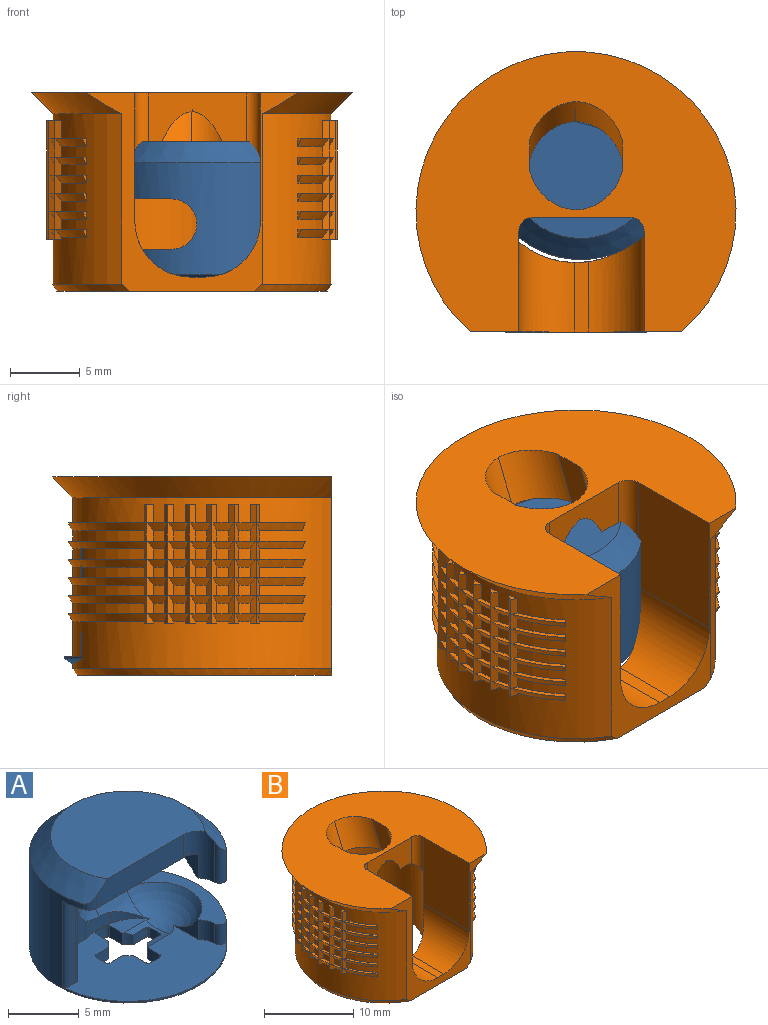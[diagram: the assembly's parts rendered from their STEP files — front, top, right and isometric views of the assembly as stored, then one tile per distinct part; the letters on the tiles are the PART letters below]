
ASSEMBLY  parts=2 mates=1
PART A: 62 faces, bbox 14.4x14.4x10.8 mm
  f0: cone r=6.37mm half-angle=55deg, axis (0,0,1), area 59.3mm2, adj f4,f50
  f1: sphere r=3.61mm, area 17.9mm2, adj f3,f6,f8,f10,f19,f29,f32
  f2: cone r=6.22mm half-angle=45deg, axis (0,0,-1), area 57.3mm2, adj f4,f36,f49,f51,f52,f53,f56
  f3: cone r=3.61mm half-angle=0deg, axis (-1,0,0), area 2.6mm2, adj f1,f8,f39,f40,f41,f42,f43,f44
  f4: cylinder r=6.98mm len=13.95mm, axis (0,0,1), area 160.7mm2, adj f0,f2,f8,f11,f18,f32,f36,f51
  f5: cylinder r=6.91mm len=2.63mm, axis (0,0,-1), area 4.8mm2, adj f7,f11,f12,f59,f60
  f6: cylinder r=3.65mm len=0.52mm, axis (0,0,-1), area 0mm2, adj f1,f8,f10
  f7: cylinder r=3.65mm len=3.82mm, axis (0,0,-1), area 4.6mm2, adj f5,f9,f11,f58,f60
  f8: plane 12.24x9.74mm, normal (0,0,1), area 68.7mm2, adj f1,f3,f4,f6,f10,f12,f13,f14
  f9: plane 2.51x2.4mm, normal (-1,-0.02,0), area 2.7mm2, adj f7,f11,f53,f57,f58
  f10: plane 1.99x1.7mm, normal (-1,-0.02,0), area 1.6mm2, adj f1,f6,f8,f32,f34
  f11: plane 10.92x5.9mm, normal (0,0,-1), area 50.1mm2, adj f4,f5,f7,f9,f12,f13,f14,f15
  f12: plane 7.4x2.64mm, normal (0,-1,0), area 17.4mm2, adj f5,f8,f11,f13,f20,f59
  f13: cylinder r=1mm len=7.4mm, axis (0,0,-1), area 9mm2, adj f8,f11,f12,f14
  f14: cylinder r=5.6mm len=7.4mm, axis (0,0,-1), area 14.7mm2, adj f8,f11,f13,f15
  f15: plane 7.4x0.4mm, normal (1,0,0), area 3mm2, adj f8,f11,f14,f16
  f16: cylinder r=0.3mm len=7.4mm, axis (0,0,-1), area 3.5mm2, adj f8,f11,f15,f17
  f17: plane 7.4x0.76mm, normal (0,-1,0), area 5.6mm2, adj f8,f11,f16,f18
  f18: cylinder r=0.3mm len=7.4mm, axis (0,0,-1), area 3.4mm2, adj f4,f8,f11,f17
  f19: cylinder r=3.65mm len=2.35mm, axis (0,0,-1), area 1.4mm2, adj f1,f8,f20,f29
  f20: cylinder r=6.91mm len=2.63mm, axis (0,0,-1), area 3.2mm2, adj f8,f12,f19,f29,f59
  f21: cylinder r=2.75mm len=1.08mm, axis (0,0,1), area 1.1mm2, adj f8,f22,f37,f50
  f22: cylinder r=0.2mm len=1mm, axis (0,0,1), area 0.3mm2, adj f8,f21,f23,f50
  f23: plane 1.29x1mm, normal (1,0,0), area 1.3mm2, adj f8,f22,f24,f50
  f24: cylinder r=1.4mm len=1mm, axis (0,0,1), area 0.7mm2, adj f8,f23,f25,f50
  f25: plane 1.29x1mm, normal (0,-1,0), area 1.3mm2, adj f8,f24,f26,f50
  f26: cylinder r=0.2mm len=1mm, axis (0,0,1), area 0.3mm2, adj f8,f25,f27,f50
  f27: cylinder r=2.75mm len=1.08mm, axis (0,0,1), area 1.1mm2, adj f8,f26,f28,f50
  f28: cylinder r=0.2mm len=1mm, axis (0,0,1), area 0.3mm2, adj f8,f27,f30,f50
  f29: cone r=3.61mm half-angle=0deg, axis (-1,0,0), area 3.9mm2, adj f1,f19,f20,f32,f59,f61
  f30: plane 1.29x1mm, normal (0,1,0), area 1.3mm2, adj f8,f28,f31,f50
  f31: cylinder r=1.4mm len=1mm, axis (0,0,1), area 0.7mm2, adj f8,f30,f33,f50
  f32: plane 11.71x6.98mm, normal (0,0,1), area 27.4mm2, adj f1,f4,f10,f29,f34,f54,f55,f61
  f33: plane 1.29x1mm, normal (1,0,0), area 1.3mm2, adj f8,f31,f35,f50
  f34: cylinder r=1.5mm len=1.7mm, axis (0,0,-1), area 2mm2, adj f8,f10,f32,f55
  f35: cylinder r=0.2mm len=1mm, axis (0,0,1), area 0.3mm2, adj f8,f33,f48,f50
  f36: cylinder r=0.8mm len=1.01mm, axis (0,0,-1), area 0.8mm2, adj f2,f4,f11,f49
  f37: cylinder r=0.2mm len=1mm, axis (0,0,1), area 0.3mm2, adj f8,f21,f38,f50
  f38: plane 1.29x1mm, normal (-1,0,0), area 1.3mm2, adj f8,f37,f39,f50
  f39: cylinder r=1.4mm len=1mm, axis (0,0,1), area 0.7mm2, adj f3,f8,f38,f40,f50
  f40: plane 1.29x0.86mm, normal (0,-1,0), area 1.1mm2, adj f3,f39,f41,f50
  f41: cylinder r=0.2mm len=0.86mm, axis (0,0,1), area 0.2mm2, adj f3,f40,f42,f50
  f42: cylinder r=2.75mm len=1.08mm, axis (0,0,1), area 0.9mm2, adj f3,f41,f43,f50
  f43: cylinder r=0.2mm len=0.86mm, axis (0,0,1), area 0.2mm2, adj f3,f42,f44,f50
  f44: plane 1.29x0.86mm, normal (0,1,0), area 1.1mm2, adj f3,f43,f45,f50
  f45: cylinder r=1.4mm len=1mm, axis (0,0,1), area 0.7mm2, adj f3,f8,f44,f46,f50
  f46: plane 1.29x1mm, normal (-1,0,0), area 1.3mm2, adj f8,f45,f47,f50
  f47: cylinder r=0.2mm len=1mm, axis (0,0,1), area 0.3mm2, adj f8,f46,f48,f50
  f48: cylinder r=2.75mm len=1.08mm, axis (0,0,1), area 1.1mm2, adj f8,f35,f47,f50
  f49: plane 8.79x2mm, normal (0,-1,0), area 17mm2, adj f2,f11,f36,f53,f56
  f50: plane 11.52x11.52mm, normal (0,0,-1), area 90.4mm2, adj f0,f21,f22,f23,f24,f25,f26,f27
  f51: cylinder r=0.5mm len=3.47mm, axis (0,0,-1), area 3.7mm2, adj f2,f4,f52,f57
  f52: plane 3.49x0.03mm, normal (-1,0,0), area 0.1mm2, adj f2,f51,f53,f57
  f53: cylinder r=1.5mm len=4.1mm, axis (0,0,-1), area 7mm2, adj f2,f9,f11,f49,f52,f56,f57
  f54: cylinder r=0.5mm len=1.7mm, axis (0,0,-1), area 2.1mm2, adj f4,f8,f32,f55
  f55: plane 1.7x0.03mm, normal (-1,0,0), area 0.1mm2, adj f8,f32,f34,f54
  f56: plane 10.95x8.96mm, normal (0,0,1), area 75.9mm2, adj f2,f49,f53
  f57: plane 11.71x6.98mm, normal (0,0,-1), area 28.8mm2, adj f4,f9,f51,f52,f53,f58,f60,f61
  f58: sphere r=3.61mm, area 14mm2, adj f7,f9,f57,f60
  f59: sphere r=3.61mm, area 4.9mm2, adj f5,f12,f20,f29,f60,f61
  f60: cone r=3.61mm half-angle=0deg, axis (-1,0,0), area 3.1mm2, adj f5,f7,f57,f58,f59,f61
  f61: cylinder r=1.8mm len=3.91mm, axis (0,-1,0), area 21.1mm2, adj f4,f29,f32,f57,f59,f60
PART B: 295 faces, bbox 23.9x22.3x16.1 mm
  f0: cone r=10.72mm half-angle=45deg, axis (0,0,1), area 114.3mm2, adj f2,f31,f32
  f1: cone r=9.83mm half-angle=30deg, axis (0,0,1), area 29.9mm2, adj f2,f32,f294
  f2: cylinder r=9.97mm len=19.95mm, axis (0,0,1), area 328.1mm2, adj f0,f1,f13,f32,f34,f35,f36,f37
  f3: cone r=10.14mm half-angle=30deg, axis (0,0,1), area 14.2mm2, adj f4,f40,f75,f260
  f4: cylinder r=9.97mm len=17.44mm, axis (0,0,1), area 15.6mm2, adj f3,f40,f75,f227
  f5: cylinder r=9.97mm len=17.44mm, axis (0,0,1), area 15.6mm2, adj f6,f40,f75,f260
  f6: cone r=10.14mm half-angle=30deg, axis (0,0,1), area 14.2mm2, adj f5,f40,f75,f190
  f7: cone r=10.14mm half-angle=30deg, axis (0,0,1), area 14.2mm2, adj f8,f40,f75,f227
  f8: cylinder r=9.97mm len=17.44mm, axis (0,0,1), area 15.6mm2, adj f7,f40,f75,f167
  f9: cone r=10.14mm half-angle=30deg, axis (0,0,1), area 14.2mm2, adj f10,f40,f75,f167
  f10: cylinder r=9.97mm len=17.44mm, axis (0,0,1), area 15.6mm2, adj f9,f40,f75,f132
  f11: cone r=10.14mm half-angle=30deg, axis (0,0,1), area 14.2mm2, adj f12,f40,f75,f132
  f12: cylinder r=9.97mm len=17.44mm, axis (0,0,1), area 15.6mm2, adj f11,f40,f75,f99
  f13: cone r=10.14mm half-angle=30deg, axis (0,0,1), area 14.2mm2, adj f2,f40,f75,f99
  f14: cylinder r=6.42mm len=12.84mm, axis (0,0,1), area 306.5mm2, adj f23,f24,f25,f26,f27,f28,f29,f33
  f15: cylinder r=3.52mm len=5.4mm, axis (0,-0.37,-0.93), area 16.8mm2, adj f16,f19,f21,f31
  f16: plane 3.69x3.5mm, normal (-1,0,0), area 8mm2, adj f15,f17,f21,f31
  f17: cylinder r=3.52mm len=5.1mm, axis (0,-0.37,-0.93), area 14.5mm2, adj f16,f18,f21,f22,f31
  f18: cylinder r=3.52mm len=5.1mm, axis (0,-0.37,-0.93), area 14.5mm2, adj f17,f20,f21,f22,f31
  f19: cylinder r=3.52mm len=5.4mm, axis (0,-0.37,-0.93), area 16.8mm2, adj f15,f20,f21,f31
  f20: plane 3.69x3.5mm, normal (1,0,0), area 8mm2, adj f18,f19,f21,f31
  f21: plane 10.17x8.62mm, normal (0,0,-1), area 27.1mm2, adj f15,f16,f17,f18,f19,f20,f22,f23
  f22: plane 7.91x4.54mm, normal (0,-1,0), area 18.2mm2, adj f17,f18,f21,f23,f29,f30,f31
  f23: cone r=5.64mm half-angle=52.3deg, axis (0,0,-1), area 50.9mm2, adj f14,f21,f22,f27,f29,f30
  f24: cylinder r=4mm len=7.25mm, axis (0,-1,0), area 38.6mm2, adj f14,f25,f28,f32
  f25: plane 5.05x1mm, normal (0,0,1), area 5mm2, adj f14,f24,f26,f32
  f26: cylinder r=4mm len=6.46mm, axis (0,-1,0), area 36mm2, adj f14,f25,f27,f32
  f27: plane 9.23x7.24mm, normal (1,0,0), area 62.8mm2, adj f14,f23,f26,f30,f31,f32
  f28: plane 9.2x7.25mm, normal (-1,0,0), area 66.4mm2, adj f14,f24,f29,f31,f32,f33
  f29: cylinder r=1mm len=5.7mm, axis (0,0,-1), area 6.6mm2, adj f14,f22,f23,f28,f31,f33
  f30: cylinder r=1mm len=4.28mm, axis (0,0,-1), area 5.9mm2, adj f21,f22,f23,f27,f31
  f31: plane 23.39x20.51mm, normal (0,0,1), area 269mm2, adj f0,f15,f16,f17,f18,f19,f20,f22
  f32: plane 15.42x14.43mm, normal (0,-1,0), area 35.3mm2, adj f0,f1,f2,f24,f25,f26,f27,f28
  f33: plane 0.05x0mm, normal (0,0,-1), area 0mm2, adj f14,f28,f29
  f34: plane 8.51x0.53mm, normal (0.37,-0.93,0), area 4.1mm2, adj f2,f54,f70,f81,f138,f160,f173,f196
  f35: plane 8.51x0.49mm, normal (0.52,-0.86,0), area 4.1mm2, adj f2,f43,f68,f71,f92,f104,f114,f125
  f36: plane 8.51x0.44mm, normal (0.64,-0.77,0), area 4.1mm2, adj f2,f44,f67,f72,f91,f103,f113,f124
  f37: plane 8.51x0.43mm, normal (0.75,-0.66,0), area 4.1mm2, adj f2,f45,f66,f73,f90,f102,f112,f123
  f38: plane 8.51x0.48mm, normal (0.85,-0.53,0), area 4.1mm2, adj f2,f46,f65,f74,f89,f101,f111,f122
  f39: plane 8.51x0.52mm, normal (0.92,-0.39,0), area 4.1mm2, adj f2,f47,f64,f75,f88,f100,f110,f121
  f40: plane 8.51x0.55mm, normal (-0.22,0.97,0), area 4.1mm2, adj f2,f3,f4,f5,f6,f7,f8,f9
  f41: plane 8.51x0.53mm, normal (-0.37,0.93,0), area 4.1mm2, adj f2,f49,f62,f77,f87,f98,f109,f120
  f42: plane 8.51x0.49mm, normal (-0.52,0.86,0), area 4.1mm2, adj f2,f50,f61,f78,f86,f97,f108,f119
  f43: plane 0.72x0.48mm, normal (0,0,-1), area 0.2mm2, adj f2,f35,f71
  f44: plane 0.72x0.43mm, normal (0,0,-1), area 0.2mm2, adj f2,f36,f72
  f45: plane 0.72x0.48mm, normal (0,0,-1), area 0.2mm2, adj f2,f37,f73
  f46: plane 0.69x0.52mm, normal (0,0,-1), area 0.2mm2, adj f2,f38,f74
  f47: plane 0.65x0.55mm, normal (0,0,-1), area 0.2mm2, adj f2,f39,f75
  f48: plane 0.65x0.55mm, normal (0,0,-1), area 0.2mm2, adj f2,f40,f76
  f49: plane 0.69x0.52mm, normal (0,0,-1), area 0.2mm2, adj f2,f41,f77
  f50: plane 0.72x0.48mm, normal (0,0,-1), area 0.2mm2, adj f2,f42,f78
  f51: plane 0.72x0.43mm, normal (0,0,-1), area 0.2mm2, adj f2,f55,f79
  f52: plane 0.72x0.48mm, normal (0,0,-1), area 0.2mm2, adj f2,f56,f80
  f53: plane 0.69x0.52mm, normal (0,0,-1), area 0.2mm2, adj f2,f57,f69
  f54: plane 0.69x0.52mm, normal (0,0,-1), area 0.2mm2, adj f2,f34,f70
  f55: plane 8.51x0.44mm, normal (-0.64,0.77,0), area 4.1mm2, adj f2,f51,f60,f79,f85,f96,f107,f118
  f56: plane 8.51x0.43mm, normal (-0.75,0.66,0), area 4.1mm2, adj f2,f52,f59,f80,f84,f95,f106,f117
  f57: plane 8.51x0.48mm, normal (-0.85,0.53,0), area 4.1mm2, adj f2,f53,f58,f69,f83,f94,f105,f116
  f58: plane 0.69x0.52mm, normal (0,0,1), area 0.2mm2, adj f2,f57,f69
  f59: plane 0.72x0.48mm, normal (0,0,1), area 0.2mm2, adj f2,f56,f80
  f60: plane 0.72x0.43mm, normal (0,0,1), area 0.2mm2, adj f2,f55,f79
  f61: plane 0.72x0.48mm, normal (0,0,1), area 0.2mm2, adj f2,f42,f78
  f62: plane 0.69x0.52mm, normal (0,0,1), area 0.2mm2, adj f2,f41,f77
  f63: plane 0.65x0.55mm, normal (0,0,1), area 0.2mm2, adj f2,f40,f76
  f64: plane 0.65x0.55mm, normal (0,0,1), area 0.2mm2, adj f2,f39,f75
  f65: plane 0.69x0.52mm, normal (0,0,1), area 0.2mm2, adj f2,f38,f74
  f66: plane 0.72x0.48mm, normal (0,0,1), area 0.2mm2, adj f2,f37,f73
  f67: plane 0.72x0.43mm, normal (0,0,1), area 0.2mm2, adj f2,f36,f72
  f68: plane 0.72x0.48mm, normal (0,0,1), area 0.2mm2, adj f2,f35,f71
  f69: plane 8.51x0.53mm, normal (-0.37,-0.93,0), area 4.1mm2, adj f2,f53,f57,f58,f82,f93,f115,f126
  f70: plane 8.51x0.48mm, normal (0.85,0.53,0), area 4.1mm2, adj f2,f34,f54,f81,f92,f104,f114,f125
  f71: plane 8.51x0.43mm, normal (0.75,0.66,0), area 4.1mm2, adj f2,f35,f43,f68,f91,f103,f113,f124
  f72: plane 8.51x0.44mm, normal (0.64,0.77,0), area 4.1mm2, adj f2,f36,f44,f67,f90,f102,f112,f123
  f73: plane 8.51x0.49mm, normal (0.52,0.86,0), area 4.1mm2, adj f2,f37,f45,f66,f89,f101,f111,f122
  f74: plane 8.51x0.53mm, normal (0.37,0.93,0), area 4.1mm2, adj f2,f38,f46,f65,f88,f100,f110,f121
  f75: plane 8.51x0.55mm, normal (0.22,0.97,0), area 4.1mm2, adj f2,f3,f4,f5,f6,f7,f8,f9
  f76: plane 8.51x0.52mm, normal (-0.92,-0.39,0), area 4.1mm2, adj f2,f40,f48,f63,f87,f98,f109,f120
  f77: plane 8.51x0.48mm, normal (-0.85,-0.53,0), area 4.1mm2, adj f2,f41,f49,f62,f86,f97,f108,f119
  f78: plane 8.51x0.43mm, normal (-0.75,-0.66,0), area 4.1mm2, adj f2,f42,f50,f61,f85,f96,f107,f118
  f79: plane 8.51x0.44mm, normal (-0.64,-0.77,0), area 4.1mm2, adj f2,f51,f55,f60,f84,f95,f106,f117
  f80: plane 8.51x0.49mm, normal (-0.52,-0.86,0), area 4.1mm2, adj f2,f52,f56,f59,f83,f94,f105,f116
  f81: plane 0.69x0.52mm, normal (0,0,1), area 0.2mm2, adj f2,f34,f70
  f82: cone r=10.14mm half-angle=30deg, axis (0,0,1), area 2.4mm2, adj f2,f69,f93,f284
  f83: cone r=10.14mm half-angle=30deg, axis (0,0,1), area 0.7mm2, adj f2,f57,f80,f94
  f84: cone r=10.14mm half-angle=30deg, axis (0,0,1), area 0.7mm2, adj f2,f56,f79,f95
  f85: cone r=10.14mm half-angle=30deg, axis (0,0,1), area 0.7mm2, adj f2,f55,f78,f96
  f86: cone r=10.14mm half-angle=30deg, axis (0,0,1), area 0.7mm2, adj f2,f42,f77,f97
  f87: cone r=10.14mm half-angle=30deg, axis (0,0,1), area 0.7mm2, adj f2,f41,f76,f98
  f88: cone r=10.14mm half-angle=30deg, axis (0,0,1), area 0.7mm2, adj f2,f39,f74,f100
  f89: cone r=10.14mm half-angle=30deg, axis (0,0,1), area 0.7mm2, adj f2,f38,f73,f101
  f90: cone r=10.14mm half-angle=30deg, axis (0,0,1), area 0.7mm2, adj f2,f37,f72,f102
  f91: cone r=10.14mm half-angle=30deg, axis (0,0,1), area 0.7mm2, adj f2,f36,f71,f103
  f92: cone r=10.14mm half-angle=30deg, axis (0,0,1), area 0.7mm2, adj f2,f35,f70,f104
  f93: plane 3.43x2.18mm, normal (0,0,1), area 1.2mm2, adj f2,f69,f82,f284
  f94: plane 1.41x0.57mm, normal (0,0,1), area 0.4mm2, adj f57,f80,f83,f105
  f95: plane 1.44x0.4mm, normal (0,0,1), area 0.4mm2, adj f56,f79,f84,f106
  f96: plane 1.44x0.4mm, normal (0,0,1), area 0.4mm2, adj f55,f78,f85,f107
  f97: plane 1.41x0.57mm, normal (0,0,1), area 0.4mm2, adj f42,f77,f86,f108
  f98: plane 1.34x0.72mm, normal (0,0,1), area 0.4mm2, adj f41,f76,f87,f109
  f99: plane 18.28x5.55mm, normal (0,0,1), area 7.1mm2, adj f12,f13,f40,f75
  f100: plane 1.34x0.72mm, normal (0,0,1), area 0.4mm2, adj f39,f74,f88,f110
  f101: plane 1.41x0.57mm, normal (0,0,1), area 0.4mm2, adj f38,f73,f89,f111
  f102: plane 1.44x0.4mm, normal (0,0,1), area 0.4mm2, adj f37,f72,f90,f112
  f103: plane 1.44x0.4mm, normal (0,0,1), area 0.4mm2, adj f36,f71,f91,f113
  f104: plane 1.41x0.57mm, normal (0,0,1), area 0.4mm2, adj f35,f70,f92,f114
  f105: cylinder r=9.97mm len=0.82mm, axis (0,0,1), area 0.6mm2, adj f57,f80,f94,f116
  f106: cylinder r=9.97mm len=0.84mm, axis (0,0,1), area 0.6mm2, adj f56,f79,f95,f117
  f107: cylinder r=9.97mm len=0.84mm, axis (0,0,1), area 0.6mm2, adj f55,f78,f96,f118
  f108: cylinder r=9.97mm len=0.82mm, axis (0,0,1), area 0.6mm2, adj f42,f77,f97,f119
  f109: cylinder r=9.97mm len=0.78mm, axis (0,0,1), area 0.6mm2, adj f41,f76,f98,f120
  f110: cylinder r=9.97mm len=0.78mm, axis (0,0,1), area 0.6mm2, adj f39,f74,f100,f121
  f111: cylinder r=9.97mm len=0.82mm, axis (0,0,1), area 0.6mm2, adj f38,f73,f101,f122
  f112: cylinder r=9.97mm len=0.84mm, axis (0,0,1), area 0.6mm2, adj f37,f72,f102,f123
  f113: cylinder r=9.97mm len=0.84mm, axis (0,0,1), area 0.6mm2, adj f36,f71,f103,f124
  f114: cylinder r=9.97mm len=0.82mm, axis (0,0,1), area 0.6mm2, adj f35,f70,f104,f125
  f115: cone r=10.14mm half-angle=30deg, axis (0,0,1), area 2.4mm2, adj f2,f69,f126,f279
  f116: cone r=10.14mm half-angle=30deg, axis (0,0,1), area 0.7mm2, adj f57,f80,f105,f127
  f117: cone r=10.14mm half-angle=30deg, axis (0,0,1), area 0.7mm2, adj f56,f79,f106,f128
  f118: cone r=10.14mm half-angle=30deg, axis (0,0,1), area 0.7mm2, adj f55,f78,f107,f129
  f119: cone r=10.14mm half-angle=30deg, axis (0,0,1), area 0.7mm2, adj f42,f77,f108,f130
  f120: cone r=10.14mm half-angle=30deg, axis (0,0,1), area 0.7mm2, adj f41,f76,f109,f131
  f121: cone r=10.14mm half-angle=30deg, axis (0,0,1), area 0.7mm2, adj f39,f74,f110,f133
  f122: cone r=10.14mm half-angle=30deg, axis (0,0,1), area 0.7mm2, adj f38,f73,f111,f134
  f123: cone r=10.14mm half-angle=30deg, axis (0,0,1), area 0.7mm2, adj f37,f72,f112,f135
  f124: cone r=10.14mm half-angle=30deg, axis (0,0,1), area 0.7mm2, adj f36,f71,f113,f136
  f125: cone r=10.14mm half-angle=30deg, axis (0,0,1), area 0.7mm2, adj f35,f70,f114,f137
  f126: plane 3.43x2.18mm, normal (0,0,1), area 1.2mm2, adj f2,f69,f115,f279
  f127: plane 1.41x0.57mm, normal (0,0,1), area 0.4mm2, adj f57,f80,f116,f139
  f128: plane 1.44x0.4mm, normal (0,0,1), area 0.4mm2, adj f56,f79,f117,f140
  f129: plane 1.44x0.4mm, normal (0,0,1), area 0.4mm2, adj f55,f78,f118,f141
  f130: plane 1.41x0.57mm, normal (0,0,1), area 0.4mm2, adj f42,f77,f119,f142
  f131: plane 1.34x0.72mm, normal (0,0,1), area 0.4mm2, adj f41,f76,f120,f143
  f132: plane 18.28x5.55mm, normal (0,0,1), area 7.1mm2, adj f10,f11,f40,f75
  f133: plane 1.34x0.72mm, normal (0,0,1), area 0.4mm2, adj f39,f74,f121,f144
  f134: plane 1.41x0.57mm, normal (0,0,1), area 0.4mm2, adj f38,f73,f122,f145
  f135: plane 1.44x0.4mm, normal (0,0,1), area 0.4mm2, adj f37,f72,f123,f146
  f136: plane 1.44x0.4mm, normal (0,0,1), area 0.4mm2, adj f36,f71,f124,f147
  f137: plane 1.41x0.57mm, normal (0,0,1), area 0.4mm2, adj f35,f70,f125,f148
  f138: plane 3.43x2.18mm, normal (0,0,1), area 1.2mm2, adj f2,f34,f289,f292
  f139: cylinder r=9.97mm len=0.82mm, axis (0,0,1), area 0.6mm2, adj f57,f80,f127,f150
  f140: cylinder r=9.97mm len=0.84mm, axis (0,0,1), area 0.6mm2, adj f56,f79,f128,f151
  f141: cylinder r=9.97mm len=0.84mm, axis (0,0,1), area 0.6mm2, adj f55,f78,f129,f152
  f142: cylinder r=9.97mm len=0.82mm, axis (0,0,1), area 0.6mm2, adj f42,f77,f130,f153
  f143: cylinder r=9.97mm len=0.78mm, axis (0,0,1), area 0.6mm2, adj f41,f76,f131,f154
  f144: cylinder r=9.97mm len=0.78mm, axis (0,0,1), area 0.6mm2, adj f39,f74,f133,f155
  f145: cylinder r=9.97mm len=0.82mm, axis (0,0,1), area 0.6mm2, adj f38,f73,f134,f156
  f146: cylinder r=9.97mm len=0.84mm, axis (0,0,1), area 0.6mm2, adj f37,f72,f135,f157
  f147: cylinder r=9.97mm len=0.84mm, axis (0,0,1), area 0.6mm2, adj f36,f71,f136,f158
  f148: cylinder r=9.97mm len=0.82mm, axis (0,0,1), area 0.6mm2, adj f35,f70,f137,f159
  f149: cone r=10.14mm half-angle=30deg, axis (0,0,1), area 2.4mm2, adj f2,f69,f161,f280
  f150: cone r=10.14mm half-angle=30deg, axis (0,0,1), area 0.7mm2, adj f57,f80,f139,f162
  f151: cone r=10.14mm half-angle=30deg, axis (0,0,1), area 0.7mm2, adj f56,f79,f140,f163
  f152: cone r=10.14mm half-angle=30deg, axis (0,0,1), area 0.7mm2, adj f55,f78,f141,f164
  f153: cone r=10.14mm half-angle=30deg, axis (0,0,1), area 0.7mm2, adj f42,f77,f142,f165
  f154: cone r=10.14mm half-angle=30deg, axis (0,0,1), area 0.7mm2, adj f41,f76,f143,f166
  f155: cone r=10.14mm half-angle=30deg, axis (0,0,1), area 0.7mm2, adj f39,f74,f144,f168
  f156: cone r=10.14mm half-angle=30deg, axis (0,0,1), area 0.7mm2, adj f38,f73,f145,f169
  f157: cone r=10.14mm half-angle=30deg, axis (0,0,1), area 0.7mm2, adj f37,f72,f146,f170
  f158: cone r=10.14mm half-angle=30deg, axis (0,0,1), area 0.7mm2, adj f36,f71,f147,f171
  f159: cone r=10.14mm half-angle=30deg, axis (0,0,1), area 0.7mm2, adj f35,f70,f148,f172
  f160: cone r=10.14mm half-angle=30deg, axis (0,0,1), area 2.4mm2, adj f2,f34,f173,f288
  f161: plane 3.43x2.18mm, normal (0,0,1), area 1.2mm2, adj f2,f69,f149,f280
  f162: plane 1.41x0.57mm, normal (0,0,1), area 0.4mm2, adj f57,f80,f150,f174
  f163: plane 1.44x0.4mm, normal (0,0,1), area 0.4mm2, adj f56,f79,f151,f175
  f164: plane 1.44x0.4mm, normal (0,0,1), area 0.4mm2, adj f55,f78,f152,f176
  f165: plane 1.41x0.57mm, normal (0,0,1), area 0.4mm2, adj f42,f77,f153,f177
  f166: plane 1.34x0.72mm, normal (0,0,1), area 0.4mm2, adj f41,f76,f154,f178
  f167: plane 18.28x5.55mm, normal (0,0,1), area 7.1mm2, adj f8,f9,f40,f75
  f168: plane 1.34x0.72mm, normal (0,0,1), area 0.4mm2, adj f39,f74,f155,f179
  f169: plane 1.41x0.57mm, normal (0,0,1), area 0.4mm2, adj f38,f73,f156,f180
  f170: plane 1.44x0.4mm, normal (0,0,1), area 0.4mm2, adj f37,f72,f157,f181
  f171: plane 1.44x0.4mm, normal (0,0,1), area 0.4mm2, adj f36,f71,f158,f182
  f172: plane 1.41x0.57mm, normal (0,0,1), area 0.4mm2, adj f35,f70,f159,f183
  f173: plane 3.43x2.18mm, normal (0,0,1), area 1.2mm2, adj f2,f34,f160,f288
  f174: cylinder r=9.97mm len=0.82mm, axis (0,0,1), area 0.6mm2, adj f57,f80,f162,f198
  f175: cylinder r=9.97mm len=0.84mm, axis (0,0,1), area 0.6mm2, adj f56,f79,f163,f199
  f176: cylinder r=9.97mm len=0.84mm, axis (0,0,1), area 0.6mm2, adj f55,f78,f164,f200
  f177: cylinder r=9.97mm len=0.82mm, axis (0,0,1), area 0.6mm2, adj f42,f77,f165,f201
  f178: cylinder r=9.97mm len=0.78mm, axis (0,0,1), area 0.6mm2, adj f41,f76,f166,f202
  f179: cylinder r=9.97mm len=0.78mm, axis (0,0,1), area 0.6mm2, adj f39,f74,f168,f203
  f180: cylinder r=9.97mm len=0.82mm, axis (0,0,1), area 0.6mm2, adj f38,f73,f169,f204
  f181: cylinder r=9.97mm len=0.84mm, axis (0,0,1), area 0.6mm2, adj f37,f72,f170,f205
  f182: cylinder r=9.97mm len=0.84mm, axis (0,0,1), area 0.6mm2, adj f36,f71,f171,f206
  f183: cylinder r=9.97mm len=0.82mm, axis (0,0,1), area 0.6mm2, adj f35,f70,f172,f207
  f184: plane 3.43x2.18mm, normal (0,0,1), area 1.2mm2, adj f2,f69,f209,f283
  f185: plane 1.41x0.57mm, normal (0,0,1), area 0.4mm2, adj f2,f57,f80,f210
  f186: plane 1.44x0.4mm, normal (0,0,1), area 0.4mm2, adj f2,f56,f79,f211
  f187: plane 1.44x0.4mm, normal (0,0,1), area 0.4mm2, adj f2,f55,f78,f212
  f188: plane 1.41x0.57mm, normal (0,0,1), area 0.4mm2, adj f2,f42,f77,f213
  f189: plane 1.34x0.72mm, normal (0,0,1), area 0.4mm2, adj f2,f41,f76,f214
  f190: plane 18.28x5.55mm, normal (0,0,1), area 7.1mm2, adj f2,f6,f40,f75
  f191: plane 1.34x0.72mm, normal (0,0,1), area 0.4mm2, adj f2,f39,f74,f215
  f192: plane 1.41x0.57mm, normal (0,0,1), area 0.4mm2, adj f2,f38,f73,f216
  f193: plane 1.44x0.4mm, normal (0,0,1), area 0.4mm2, adj f2,f37,f72,f217
  f194: plane 1.44x0.4mm, normal (0,0,1), area 0.4mm2, adj f2,f36,f71,f218
  f195: plane 1.41x0.57mm, normal (0,0,1), area 0.4mm2, adj f2,f35,f70,f219
  f196: plane 3.43x2.18mm, normal (0,0,1), area 1.2mm2, adj f2,f34,f220,f285
  f197: cone r=10.14mm half-angle=30deg, axis (0,0,1), area 2.4mm2, adj f2,f69,f221,f281
  f198: cone r=10.14mm half-angle=30deg, axis (0,0,1), area 0.7mm2, adj f57,f80,f174,f222
  f199: cone r=10.14mm half-angle=30deg, axis (0,0,1), area 0.7mm2, adj f56,f79,f175,f223
  f200: cone r=10.14mm half-angle=30deg, axis (0,0,1), area 0.7mm2, adj f55,f78,f176,f224
  f201: cone r=10.14mm half-angle=30deg, axis (0,0,1), area 0.7mm2, adj f42,f77,f177,f225
  f202: cone r=10.14mm half-angle=30deg, axis (0,0,1), area 0.7mm2, adj f41,f76,f178,f226
  f203: cone r=10.14mm half-angle=30deg, axis (0,0,1), area 0.7mm2, adj f39,f74,f179,f228
  f204: cone r=10.14mm half-angle=30deg, axis (0,0,1), area 0.7mm2, adj f38,f73,f180,f229
  f205: cone r=10.14mm half-angle=30deg, axis (0,0,1), area 0.7mm2, adj f37,f72,f181,f230
  f206: cone r=10.14mm half-angle=30deg, axis (0,0,1), area 0.7mm2, adj f36,f71,f182,f231
  f207: cone r=10.14mm half-angle=30deg, axis (0,0,1), area 0.7mm2, adj f35,f70,f183,f232
  f208: cone r=10.14mm half-angle=30deg, axis (0,0,1), area 2.4mm2, adj f2,f34,f233,f287
  f209: cone r=10.14mm half-angle=30deg, axis (0,0,1), area 2.4mm2, adj f2,f69,f184,f283
  f210: cone r=10.14mm half-angle=30deg, axis (0,0,1), area 0.7mm2, adj f57,f80,f185,f234
  f211: cone r=10.14mm half-angle=30deg, axis (0,0,1), area 0.7mm2, adj f56,f79,f186,f235
  f212: cone r=10.14mm half-angle=30deg, axis (0,0,1), area 0.7mm2, adj f55,f78,f187,f236
  f213: cone r=10.14mm half-angle=30deg, axis (0,0,1), area 0.7mm2, adj f42,f77,f188,f237
  f214: cone r=10.14mm half-angle=30deg, axis (0,0,1), area 0.7mm2, adj f41,f76,f189,f238
  f215: cone r=10.14mm half-angle=30deg, axis (0,0,1), area 0.7mm2, adj f39,f74,f191,f239
  f216: cone r=10.14mm half-angle=30deg, axis (0,0,1), area 0.7mm2, adj f38,f73,f192,f240
  f217: cone r=10.14mm half-angle=30deg, axis (0,0,1), area 0.7mm2, adj f37,f72,f193,f241
  f218: cone r=10.14mm half-angle=30deg, axis (0,0,1), area 0.7mm2, adj f36,f71,f194,f242
  f219: cone r=10.14mm half-angle=30deg, axis (0,0,1), area 0.7mm2, adj f35,f70,f195,f243
  f220: cone r=10.14mm half-angle=30deg, axis (0,0,1), area 2.4mm2, adj f2,f34,f196,f285
  f221: plane 3.43x2.18mm, normal (0,0,1), area 1.2mm2, adj f2,f69,f197,f281
  f222: plane 1.41x0.57mm, normal (0,0,1), area 0.4mm2, adj f57,f80,f198,f244
  f223: plane 1.44x0.4mm, normal (0,0,1), area 0.4mm2, adj f56,f79,f199,f245
  f224: plane 1.44x0.4mm, normal (0,0,1), area 0.4mm2, adj f55,f78,f200,f246
  f225: plane 1.41x0.57mm, normal (0,0,1), area 0.4mm2, adj f42,f77,f201,f247
  f226: plane 1.34x0.72mm, normal (0,0,1), area 0.4mm2, adj f41,f76,f202,f248
  f227: plane 18.28x5.55mm, normal (0,0,1), area 7.1mm2, adj f4,f7,f40,f75
  f228: plane 1.34x0.72mm, normal (0,0,1), area 0.4mm2, adj f39,f74,f203,f249
  f229: plane 1.41x0.57mm, normal (0,0,1), area 0.4mm2, adj f38,f73,f204,f250
  f230: plane 1.44x0.4mm, normal (0,0,1), area 0.4mm2, adj f37,f72,f205,f251
  f231: plane 1.44x0.4mm, normal (0,0,1), area 0.4mm2, adj f36,f71,f206,f252
  f232: plane 1.41x0.57mm, normal (0,0,1), area 0.4mm2, adj f35,f70,f207,f253
  f233: plane 3.43x2.18mm, normal (0,0,1), area 1.2mm2, adj f2,f34,f208,f287
  f234: cylinder r=9.97mm len=0.82mm, axis (0,0,1), area 0.6mm2, adj f57,f80,f210,f255
  f235: cylinder r=9.97mm len=0.84mm, axis (0,0,1), area 0.6mm2, adj f56,f79,f211,f256
  f236: cylinder r=9.97mm len=0.84mm, axis (0,0,1), area 0.6mm2, adj f55,f78,f212,f257
  f237: cylinder r=9.97mm len=0.82mm, axis (0,0,1), area 0.6mm2, adj f42,f77,f213,f258
  f238: cylinder r=9.97mm len=0.78mm, axis (0,0,1), area 0.6mm2, adj f41,f76,f214,f259
  f239: cylinder r=9.97mm len=0.78mm, axis (0,0,1), area 0.6mm2, adj f39,f74,f215,f261
  f240: cylinder r=9.97mm len=0.82mm, axis (0,0,1), area 0.6mm2, adj f38,f73,f216,f262
  f241: cylinder r=9.97mm len=0.84mm, axis (0,0,1), area 0.6mm2, adj f37,f72,f217,f263
  f242: cylinder r=9.97mm len=0.84mm, axis (0,0,1), area 0.6mm2, adj f36,f71,f218,f264
  f243: cylinder r=9.97mm len=0.82mm, axis (0,0,1), area 0.6mm2, adj f35,f70,f219,f265
  f244: cylinder r=9.97mm len=0.82mm, axis (0,0,1), area 0.6mm2, adj f57,f80,f222,f268
  f245: cylinder r=9.97mm len=0.84mm, axis (0,0,1), area 0.6mm2, adj f56,f79,f223,f269
  f246: cylinder r=9.97mm len=0.84mm, axis (0,0,1), area 0.6mm2, adj f55,f78,f224,f270
  f247: cylinder r=9.97mm len=0.82mm, axis (0,0,1), area 0.6mm2, adj f42,f77,f225,f271
  f248: cylinder r=9.97mm len=0.78mm, axis (0,0,1), area 0.6mm2, adj f41,f76,f226,f272
  f249: cylinder r=9.97mm len=0.78mm, axis (0,0,1), area 0.6mm2, adj f39,f74,f228,f273
  f250: cylinder r=9.97mm len=0.82mm, axis (0,0,1), area 0.6mm2, adj f38,f73,f229,f274
  f251: cylinder r=9.97mm len=0.84mm, axis (0,0,1), area 0.6mm2, adj f37,f72,f230,f275
  f252: cylinder r=9.97mm len=0.84mm, axis (0,0,1), area 0.6mm2, adj f36,f71,f231,f276
  f253: cylinder r=9.97mm len=0.82mm, axis (0,0,1), area 0.6mm2, adj f35,f70,f232,f277
  f254: plane 3.43x2.18mm, normal (0,0,1), area 1.2mm2, adj f2,f69,f267,f282
  f255: plane 1.41x0.57mm, normal (0,0,1), area 0.4mm2, adj f57,f80,f234,f268
  f256: plane 1.44x0.4mm, normal (0,0,1), area 0.4mm2, adj f56,f79,f235,f269
  f257: plane 1.44x0.4mm, normal (0,0,1), area 0.4mm2, adj f55,f78,f236,f270
  f258: plane 1.41x0.57mm, normal (0,0,1), area 0.4mm2, adj f42,f77,f237,f271
  f259: plane 1.34x0.72mm, normal (0,0,1), area 0.4mm2, adj f41,f76,f238,f272
  f260: plane 18.28x5.55mm, normal (0,0,1), area 7.1mm2, adj f3,f5,f40,f75
  f261: plane 1.34x0.72mm, normal (0,0,1), area 0.4mm2, adj f39,f74,f239,f273
  f262: plane 1.41x0.57mm, normal (0,0,1), area 0.4mm2, adj f38,f73,f240,f274
  f263: plane 1.44x0.4mm, normal (0,0,1), area 0.4mm2, adj f37,f72,f241,f275
  f264: plane 1.44x0.4mm, normal (0,0,1), area 0.4mm2, adj f36,f71,f242,f276
  f265: plane 1.41x0.57mm, normal (0,0,1), area 0.4mm2, adj f35,f70,f243,f277
  f266: plane 3.43x2.18mm, normal (0,0,1), area 1.2mm2, adj f2,f34,f278,f286
  f267: cone r=10.14mm half-angle=30deg, axis (0,0,1), area 2.4mm2, adj f2,f69,f254,f282
  f268: cone r=10.14mm half-angle=30deg, axis (0,0,1), area 0.7mm2, adj f57,f80,f244,f255
  f269: cone r=10.14mm half-angle=30deg, axis (0,0,1), area 0.7mm2, adj f56,f79,f245,f256
  f270: cone r=10.14mm half-angle=30deg, axis (0,0,1), area 0.7mm2, adj f55,f78,f246,f257
  f271: cone r=10.14mm half-angle=30deg, axis (0,0,1), area 0.7mm2, adj f42,f77,f247,f258
  f272: cone r=10.14mm half-angle=30deg, axis (0,0,1), area 0.7mm2, adj f41,f76,f248,f259
  f273: cone r=10.14mm half-angle=30deg, axis (0,0,1), area 0.7mm2, adj f39,f74,f249,f261
  f274: cone r=10.14mm half-angle=30deg, axis (0,0,1), area 0.7mm2, adj f38,f73,f250,f262
  f275: cone r=10.14mm half-angle=30deg, axis (0,0,1), area 0.7mm2, adj f37,f72,f251,f263
  f276: cone r=10.14mm half-angle=30deg, axis (0,0,1), area 0.7mm2, adj f36,f71,f252,f264
  f277: cone r=10.14mm half-angle=30deg, axis (0,0,1), area 0.7mm2, adj f35,f70,f253,f265
  f278: cone r=10.14mm half-angle=30deg, axis (0,0,1), area 2.4mm2, adj f2,f34,f266,f286
  f279: plane 0.56x0.25mm, normal (0.65,-0.76,0), area 0.1mm2, adj f2,f115,f126
  f280: plane 0.56x0.25mm, normal (0.65,-0.76,0), area 0.1mm2, adj f2,f149,f161
  f281: plane 0.56x0.25mm, normal (0.65,-0.76,0), area 0.1mm2, adj f2,f197,f221
  f282: plane 0.56x0.25mm, normal (0.65,-0.76,0), area 0.1mm2, adj f2,f254,f267
  f283: plane 0.56x0.25mm, normal (0.65,-0.76,0), area 0.1mm2, adj f2,f184,f209
  f284: plane 0.56x0.25mm, normal (0.65,-0.76,0), area 0.1mm2, adj f2,f82,f93
  f285: plane 0.56x0.25mm, normal (-0.65,-0.76,0), area 0.1mm2, adj f2,f196,f220
  f286: plane 0.56x0.25mm, normal (-0.65,-0.76,0), area 0.1mm2, adj f2,f266,f278
  f287: plane 0.56x0.25mm, normal (-0.65,-0.76,0), area 0.1mm2, adj f2,f208,f233
  f288: plane 0.56x0.25mm, normal (-0.65,-0.76,0), area 0.1mm2, adj f2,f160,f173
  f289: plane 0.56x0.25mm, normal (-0.65,-0.76,0), area 0.1mm2, adj f2,f138,f292
  f290: cone r=10.14mm half-angle=30deg, axis (0,0,1), area 2.4mm2, adj f2,f34,f291,f293
  f291: plane 3.43x2.18mm, normal (0,0,1), area 1.2mm2, adj f2,f34,f290,f293
  f292: cone r=10.14mm half-angle=30deg, axis (0,0,1), area 2.4mm2, adj f2,f34,f138,f289
  f293: plane 0.56x0.25mm, normal (-0.65,-0.76,0), area 0.1mm2, adj f2,f290,f291
  f294: plane 19.37x18.29mm, normal (0,0,-1), area 158.8mm2, adj f1,f14,f32
PLACE A rot(axis=(0,0,1),165deg) t=(1.65,22.37,4.98)mm
PLACE B t=(0.57,16.11,4.98)mm
MATE revolute A.f56 <-> B.f21  axis (0,0,1) through (0.66,18.78,1.48)mm
